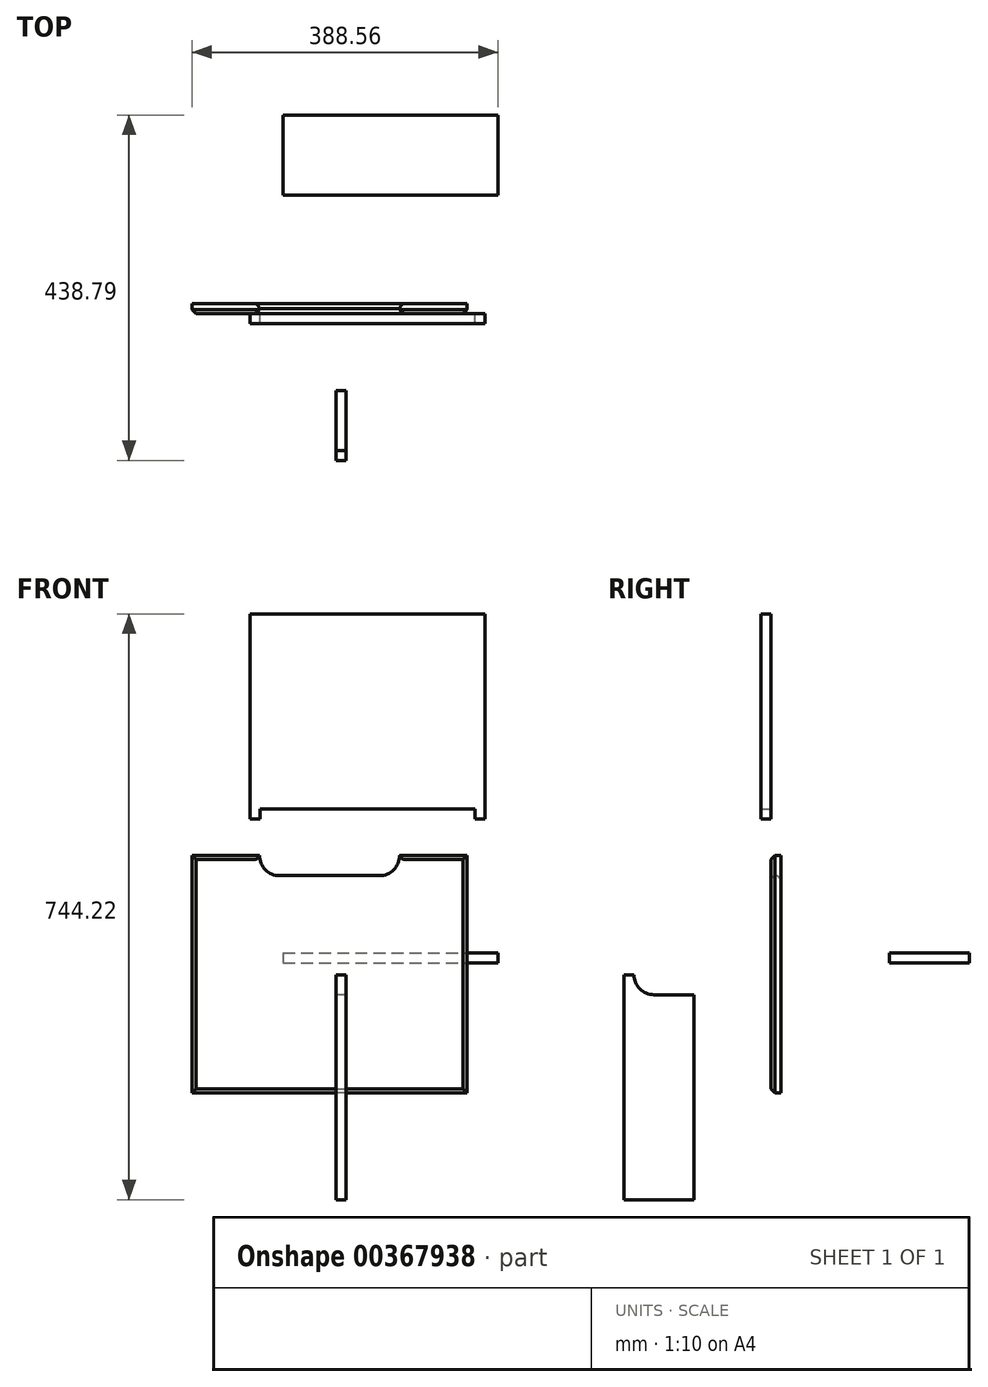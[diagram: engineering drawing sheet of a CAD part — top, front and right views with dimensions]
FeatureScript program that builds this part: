
annotation { "Feature Type Name" : "Feature", "Feature Type Description" : "" }
export const myFeature = defineFeature(function(context is Context, id is Id, definition is map)
    precondition{}
    {
        {
            var Q0;
            Q0=qCreatedBy(makeId("Front.planeOp"),FACE);
            var sketch = newSketch(context, id + "F0", { "sketchPlane" : qUnion([Q0])});
            skLineSegment(sketch, "E0.bottom", {"start": v(-182.85, 136.03) * mm, "end": v(-97.13, 136.03) * mm});
            skLineSegment(sketch, "E0.top", {"start": v(-182.85, -165.6) * mm, "end": v(166.4, -165.6) * mm});
            skLineSegment(sketch, "E0.left", {"start": v(-182.85, 136.03) * mm, "end": v(-182.85, -165.6) * mm});
            skLineSegment(sketch, "E0.right", {"start": v(166.4, 136.03) * mm, "end": v(166.4, -165.6) * mm});
            skArc(sketch, "E1.0.startCap", {"start": v(-71.73, 110.63) * mm, "mid": v(-89.69, 118.07) * mm, "end": v(-97.13, 136.03) * mm});
            skArc(sketch, "E1.0.endCap", {"start": v(80.67, 136.03) * mm, "mid": v(73.23, 118.07) * mm, "end": v(55.27, 110.63) * mm});
            skLineSegment(sketch, "E1.0.right", {"start": v(-71.73, 110.63) * mm, "end": v(55.27, 110.63) * mm});
            skLineSegment(sketch, "E2.trimOffspring", {"start": v(80.67, 136.03) * mm, "end": v(166.4, 136.03) * mm});
            skSolve(sketch);
        }
        {
            var Q0;
            Q0=makeQuery(id+"F0.imprint","IMPRINT",FACE,{"disambiguationData":[TD([[makeQuery(id+"F0.imprint","IMPRINT",EDGE,{"derivedFrom":sQuery(id+"F0.wireOp",EDGE,"E0.bottom")}),-1.0]])]});
            extrude(context, id + "F1", {"entities" : qUnion([Q0]), "depth" : 12.7 * mm});
        }
        {
            var Q0;
            Q0=makeQuery(id+"F1.opExtrude","CAP_EDGE",EDGE,{"disambiguationData":[OSD([sQuery(id+"F0.wireOp",EDGE,"E0.top")])],"isStart":false});
            var Q1;
            Q1=makeQuery(id+"F1.opExtrude","CAP_EDGE",EDGE,{"disambiguationData":[OSD([sQuery(id+"F0.wireOp",EDGE,"E0.right")])],"isStart":false});
            var Q2;
            Q2=makeQuery(id+"F1.opExtrude","CAP_EDGE",EDGE,{"disambiguationData":[OSD([sQuery(id+"F0.wireOp",EDGE,"E0.left")])],"isStart":false});
            var Q3;
            Q3=makeQuery(id+"F1.opExtrude","CAP_EDGE",EDGE,{"disambiguationData":[OSD([sQuery(id+"F0.wireOp",EDGE,"E0.bottom")])],"isStart":false});
            var Q4;
            Q4=makeQuery(id+"F1.opExtrude","CAP_EDGE",EDGE,{"disambiguationData":[OSD([sQuery(id+"F0.wireOp",EDGE,"E2.trimOffspring")])],"isStart":false});
            chamfer(context, id + "F2", {"entities" : qUnion([Q0, Q1, Q2, Q3, Q4]), "width" : 5.08 * mm});
        }
        {
            var Q0;
            Q0=makeQuery(id+"F1.opExtrude","CAP_EDGE",EDGE,{"disambiguationData":[OSD([sQuery(id+"F0.wireOp",EDGE,"E1.0.right")])],"isStart":false});
            var Q1;
            Q1=makeQuery(id+"F1.opExtrude","CAP_EDGE",EDGE,{"disambiguationData":[OSD([sQuery(id+"F0.wireOp",EDGE,"E1.0.right")])],"isStart":true});
            fillet(context, id + "F3", {"entities" : qUnion([Q0, Q1]), "radius" : 7.62 * mm, "tangentPropagation" : true, "allowEdgeOverflow" : false});
        }
        {
            var Q0;
            Q0=qCreatedBy(makeId("Top.planeOp"),FACE);
            var sketch = newSketch(context, id + "F4", { "sketchPlane" : qUnion([Q0])});
            skLineSegment(sketch, "E3.bottom", {"start": v(-67.34, 137.9) * mm, "end": v(205.7, 137.9) * mm});
            skLineSegment(sketch, "E3.top", {"start": v(-67.34, 239.5) * mm, "end": v(205.7, 239.5) * mm});
            skLineSegment(sketch, "E3.left", {"start": v(-67.34, 137.9) * mm, "end": v(-67.34, 239.5) * mm});
            skLineSegment(sketch, "E3.right", {"start": v(205.7, 137.9) * mm, "end": v(205.7, 239.5) * mm});
            skSolve(sketch);
        }
        {
            var Q0;
            Q0=makeQuery(id+"F4.imprint","IMPRINT",FACE,{"disambiguationData":[TD([[makeQuery(id+"F4.imprint","IMPRINT",EDGE,{"derivedFrom":sQuery(id+"F4.wireOp",EDGE,"E3.bottom")}),1.0]])]});
            extrude(context, id + "F5", {"entities" : qUnion([Q0]), "depth" : 12.7 * mm});
        }
        {
            var Q0;
            Q0=qCreatedBy(makeId("Right.planeOp"),FACE);
            var sketch = newSketch(context, id + "F6", { "sketchPlane" : qUnion([Q0])});
            skLineSegment(sketch, "E4.bottom", {"start": v(-186.6, -15.31) * mm, "end": v(-199.3, -15.31) * mm});
            skLineSegment(sketch, "E4.top", {"start": v(-110.4, -301.06) * mm, "end": v(-199.3, -301.06) * mm});
            skLineSegment(sketch, "E4.left", {"start": v(-110.4, -40.71) * mm, "end": v(-110.4, -301.06) * mm});
            skLineSegment(sketch, "E4.right", {"start": v(-199.3, -15.31) * mm, "end": v(-199.3, -301.06) * mm});
            skArc(sketch, "E5.0.startCap", {"start": v(-161.2, -40.71) * mm, "mid": v(-179.15, -33.27) * mm, "end": v(-186.6, -15.31) * mm});
            skLineSegment(sketch, "E5.0.right", {"start": v(-161.2, -40.71) * mm, "end": v(-110.4, -40.71) * mm});
            skPoint(sketch, "E6.orphan", {"position": v(-110.4, -15.31) * mm});
            skSolve(sketch);
        }
        {
            var Q0;
            Q0=makeQuery(id+"F6.imprint","IMPRINT",FACE,{"disambiguationData":[TD([[makeQuery(id+"F6.imprint","IMPRINT",EDGE,{"derivedFrom":sQuery(id+"F6.wireOp",EDGE,"E4.bottom")}),1.0]])]});
            extrude(context, id + "F7", {"entities" : qUnion([Q0]), "depth" : 12.7 * mm});
        }
        {
            var Q0;
            Q0=makeQuery(id+"F1.opExtrude","CAP_FACE",FACE,{"disambiguationData":[OSD([sQuery(id+"F0.wireOp",EDGE,"E0.bottom"),sQuery(id+"F0.wireOp",EDGE,"E0.top"),sQuery(id+"F0.wireOp",EDGE,"E0.left"),sQuery(id+"F0.wireOp",EDGE,"E0.right"),sQuery(id+"F0.wireOp",EDGE,"E1.0.startCap"),sQuery(id+"F0.wireOp",EDGE,"E1.0.endCap"),sQuery(id+"F0.wireOp",EDGE,"E1.0.right"),sQuery(id+"F0.wireOp",EDGE,"E2.trimOffspring")])],"isStart":false});
            var sketch = newSketch(context, id + "F8", { "sketchPlane" : qUnion([Q0])});
            skLineSegment(sketch, "E7.bottom", {"start": v(-109.28, 443.16) * mm, "end": v(189.17, 443.16) * mm});
            skLineSegment(sketch, "E7.top", {"start": v(-96.58, 195.5) * mm, "end": v(176.47, 195.5) * mm});
            skLineSegment(sketch, "E7.left", {"start": v(-109.28, 443.16) * mm, "end": v(-109.28, 195.5) * mm});
            skLineSegment(sketch, "E7.right", {"start": v(189.17, 443.16) * mm, "end": v(189.17, 195.5) * mm});
            skLineSegment(sketch, "E8.top", {"start": v(189.17, 182.8) * mm, "end": v(176.47, 182.8) * mm});
            skLineSegment(sketch, "E8.left", {"start": v(189.17, 195.5) * mm, "end": v(189.17, 182.8) * mm});
            skLineSegment(sketch, "E8.right", {"start": v(176.47, 195.5) * mm, "end": v(176.47, 182.8) * mm});
            skLineSegment(sketch, "E9.top", {"start": v(-109.28, 182.8) * mm, "end": v(-96.58, 182.8) * mm});
            skLineSegment(sketch, "E9.left", {"start": v(-109.28, 195.5) * mm, "end": v(-109.28, 182.8) * mm});
            skLineSegment(sketch, "E9.right", {"start": v(-96.58, 195.5) * mm, "end": v(-96.58, 182.8) * mm});
            skSolve(sketch);
        }
        {
            var Q0;
            Q0=makeQuery(id+"F8.imprint","IMPRINT",FACE,{"disambiguationData":[TD([[makeQuery(id+"F8.imprint","IMPRINT",EDGE,{"derivedFrom":sQuery(id+"F8.wireOp",EDGE,"E7.bottom")}),-1.0]])]});
            extrude(context, id + "F9", {"entities" : qUnion([Q0]), "depth" : 12.7 * mm});
        }
    });
